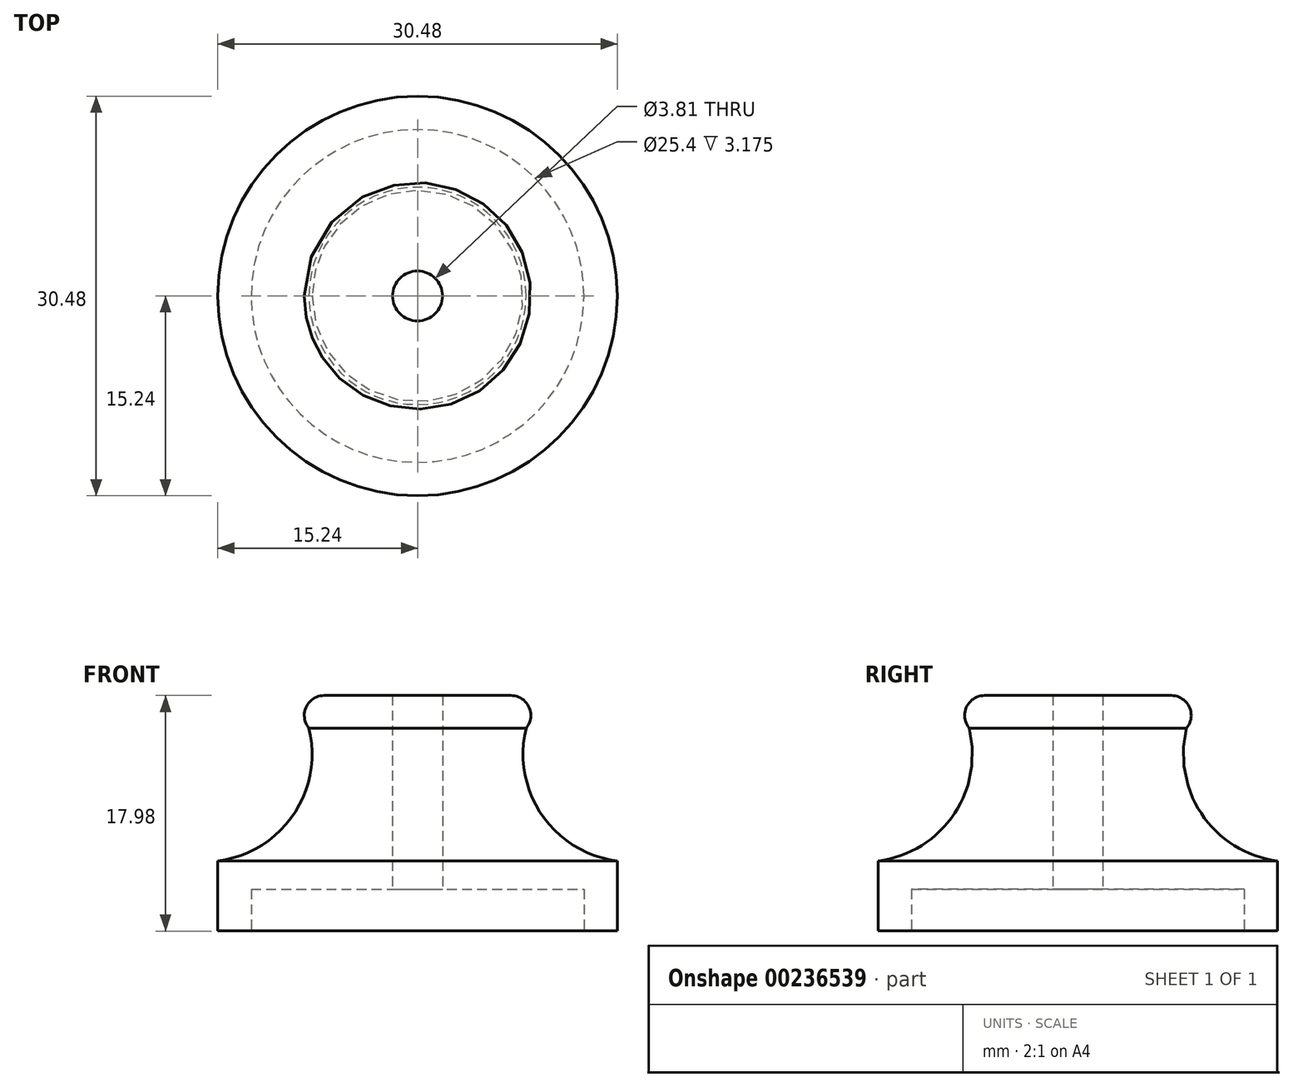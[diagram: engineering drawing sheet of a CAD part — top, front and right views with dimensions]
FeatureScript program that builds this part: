
annotation { "Feature Type Name" : "Feature", "Feature Type Description" : "" }
export const myFeature = defineFeature(function(context is Context, id is Id, definition is map)
    precondition{}
    {
        {
            var Q0;
            Q0=qCreatedBy(makeId("Front.planeOp"),FACE);
            var sketch = newSketch(context, id + "F0", { "sketchPlane" : qUnion([Q0])});
            skLineSegment(sketch, "E0", {"start": v(0, 0) * mm, "end": v(0, 9.37) * mm, "construction": true});
            skLineSegment(sketch, "E1", {"start": v(1.9, 14.8) * mm, "end": v(1.9, 0) * mm});
            skLineSegment(sketch, "E2", {"start": v(1.9, 0) * mm, "end": v(12.7, 0) * mm});
            skLineSegment(sketch, "E3", {"start": v(12.7, 0) * mm, "end": v(12.7, -3.18) * mm});
            skLineSegment(sketch, "E4", {"start": v(12.7, -3.17) * mm, "end": v(15.24, -3.17) * mm});
            skLineSegment(sketch, "E5", {"start": v(15.24, -3.18) * mm, "end": v(15.24, 2.17) * mm});
            skArc(sketch, "E6", {"start": v(8.29, 12.3) * mm, "mid": v(9.5, 5.68) * mm, "end": v(15.24, 2.17) * mm});
            skLineSegment(sketch, "E7", {"start": v(1.9, 14.8) * mm, "end": v(7.13, 14.8) * mm});
            skArc(sketch, "E8", {"start": v(7.13, 14.8) * mm, "mid": v(8.5, 13.92) * mm, "end": v(8.29, 12.3) * mm});
            skSolve(sketch);
        }
        {
            var Q0;
            Q0=makeQuery(id+"F0.imprint","IMPRINT",FACE,{"disambiguationData":[TD([[makeQuery(id+"F0.imprint","IMPRINT",EDGE,{"derivedFrom":sQuery(id+"F0.wireOp",EDGE,"E1")}),1.0]])]});
            var Q1;
            Q1=sQuery(id+"F0.wireOp",EDGE,"E0");
            revolve(context, id + "F1", {"entities" : qUnion([Q0]), "axis" : qUnion([Q1]), "revolveType" : RevolveType.FULL});
        }
    });
